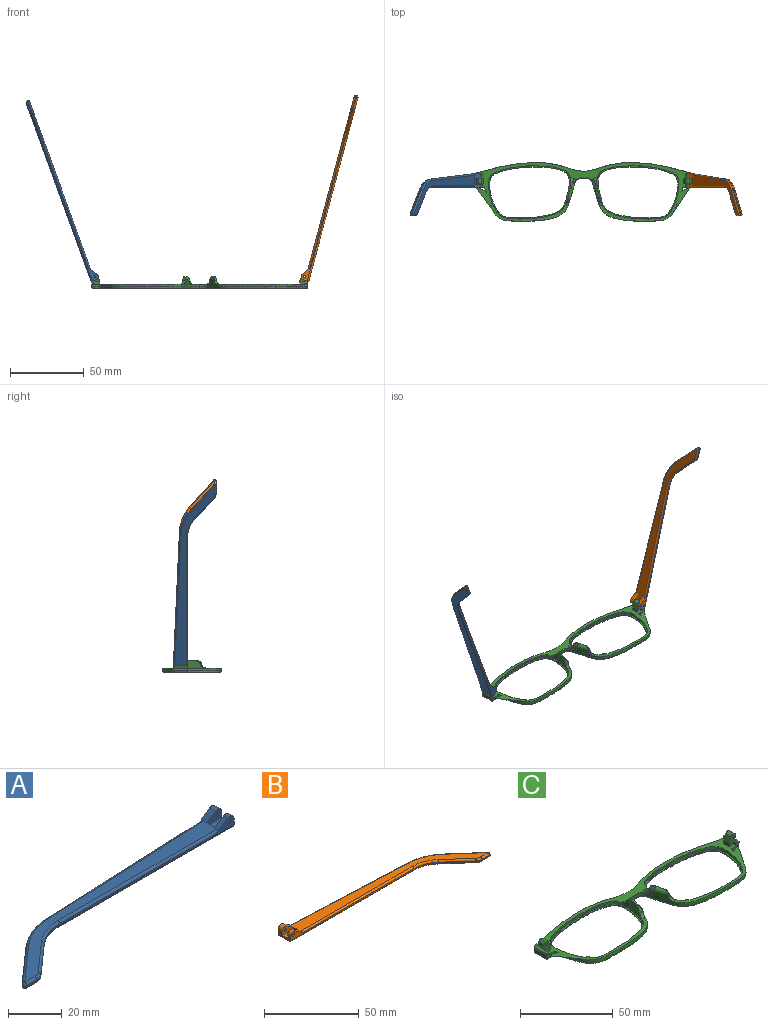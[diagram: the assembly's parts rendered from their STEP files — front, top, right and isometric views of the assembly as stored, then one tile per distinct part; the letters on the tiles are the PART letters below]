
ASSEMBLY  parts=3 mates=2
PART A: 43 faces, bbox 130.2x29.5x5.9 mm
  f0: plane 9.62x3.72mm, normal (1,0,0), area 24.7mm2, adj f1,f3,f4,f5,f10,f16,f18,f28
  f1: cylinder r=2.2mm len=3.45mm, axis (0,-1,0), area 11mm2, adj f0,f2,f4,f37
  f2: plane 6.01x3.91mm, normal (-0.55,0,0.84), area 12.7mm2, adj f1,f4,f9,f19,f37
  f3: plane 2.26x0.1mm, normal (0,0,1), area 0.1mm2, adj f0,f5,f18
  f4: plane 92.1x4.9mm, normal (0,-1,0), area 79.9mm2, adj f0,f1,f2,f14,f19,f36,f42
  f5: plane 93.42x4.13mm, normal (-0.04,1,0), area 64.8mm2, adj f0,f3,f11,f15,f17,f27,f28
  f6: plane 17.82x15.72mm, normal (-0.66,0.75,0), area 14.3mm2, adj f11,f12,f25,f30
  f7: plane 5.46x0.6mm, normal (0,-1,0), area 3.3mm2, adj f12,f13,f23,f32
  f8: plane 14.99x13.23mm, normal (0.66,-0.75,0), area 12mm2, adj f13,f14,f21,f34
  f9: plane 121.18x26.73mm, normal (0,0,1), area 627.7mm2, adj f2,f17,f19,f20,f21,f22,f23,f25
  f10: plane 129.1x27.08mm, normal (0,0,-1), area 686.5mm2, adj f0,f28,f29,f30,f32,f33,f34,f35
  f11: cylinder r=30mm len=18.52mm, axis (0,0,-1), area 12.2mm2, adj f5,f6,f26,f29
  f12: cylinder r=1mm len=1.75mm, axis (0,0,-1), area 1.5mm2, adj f6,f7,f24,f31
  f13: cylinder r=5mm len=3.31mm, axis (0,0,-1), area 2.2mm2, adj f7,f8,f22,f33
  f14: cylinder r=20mm len=13.23mm, axis (0,0,1), area 8.7mm2, adj f4,f8,f20,f35
  f15: plane 5.66x0.25mm, normal (0,0,-1), area 0.7mm2, adj f5,f17,f18
  f16: cylinder r=2.2mm len=3.45mm, axis (0,-1,0), area 14.8mm2, adj f0,f17,f18,f38
  f17: plane 6.01x3.91mm, normal (-0.55,0,0.84), area 16.9mm2, adj f5,f9,f15,f16,f18,f27,f38
  f18: plane 7.92x3.3mm, normal (0,1,0), area 15.9mm2, adj f0,f3,f15,f16,f17,f41
  f19: cylinder r=1mm len=84.18mm, axis (-1,0,0), area 131.4mm2, adj f2,f4,f9,f20
  f20: torus R=21mm, axis (0,0,1), area 23.1mm2, adj f9,f14,f19,f21
  f21: cylinder r=1mm len=15.65mm, axis (-0.75,-0.66,0), area 31.4mm2, adj f8,f9,f20,f22
  f22: torus R=4mm, axis (0,0,1), area 5.3mm2, adj f9,f13,f21,f23
  f23: cylinder r=1mm len=5.46mm, axis (-1,0,0), area 8.6mm2, adj f7,f9,f22,f24
  f24: sphere r=1mm, area 2.4mm2, adj f12,f23,f25
  f25: cylinder r=1mm len=18.48mm, axis (0.75,0.66,0), area 37.3mm2, adj f6,f9,f24,f26
  f26: torus R=29mm, axis (0,0,1), area 31.6mm2, adj f9,f11,f25,f27
  f27: cylinder r=1mm len=85.5mm, axis (1,0.04,0), area 133.5mm2, adj f5,f9,f17,f26
  f28: cylinder r=1mm len=93.46mm, axis (-1,-0.04,0), area 146.9mm2, adj f0,f5,f10,f29
  f29: torus R=29mm, axis (0,0,1), area 31.6mm2, adj f10,f11,f28,f30
  f30: cylinder r=1mm len=18.48mm, axis (-0.75,-0.66,0), area 37.3mm2, adj f6,f10,f29,f31
  f31: sphere r=1mm, area 2.4mm2, adj f12,f30,f32
  f32: cylinder r=1mm len=5.46mm, axis (1,0,0), area 8.6mm2, adj f7,f10,f31,f33
  f33: torus R=4mm, axis (0,0,1), area 5.3mm2, adj f10,f13,f32,f34
  f34: cylinder r=1mm len=15.65mm, axis (0.75,0.66,0), area 31.4mm2, adj f8,f10,f33,f35
  f35: torus R=21mm, axis (0,0,1), area 23.1mm2, adj f10,f14,f34,f36
  f36: cylinder r=1mm len=92.1mm, axis (1,0,0), area 144.7mm2, adj f0,f4,f10,f35
  f37: plane 7.92x4.7mm, normal (0,1,0), area 27mm2, adj f0,f1,f2,f39,f40,f42
  f38: plane 7.92x4.7mm, normal (0,-1,0), area 27mm2, adj f0,f16,f17,f39,f40,f41
  f39: plane 7.92x4.1mm, normal (0,0,1), area 32.5mm2, adj f0,f37,f38,f40
  f40: plane 4.1x1.4mm, normal (1,0,0), area 5.7mm2, adj f9,f37,f38,f39
  f41: cylinder r=0.5mm len=3.1mm, axis (0,-1,0), area 9.7mm2, adj f18,f38
  f42: cylinder r=0.5mm len=2.3mm, axis (0,-1,0), area 7.2mm2, adj f4,f37
PART B: 43 faces, bbox 130.2x29.5x5.9 mm
  f0: plane 9.62x3.72mm, normal (-1,0,0), area 24.7mm2, adj f1,f3,f4,f5,f10,f16,f18,f28
  f1: cylinder r=2.2mm len=3.45mm, axis (0,-1,0), area 11mm2, adj f0,f2,f4,f37
  f2: plane 6.01x3.91mm, normal (0.55,0,0.84), area 12.7mm2, adj f1,f4,f9,f19,f37
  f3: plane 2.26x0.1mm, normal (0,0,1), area 0.1mm2, adj f0,f5,f18
  f4: plane 92.1x4.9mm, normal (0,-1,0), area 78.2mm2, adj f0,f1,f2,f14,f19,f36,f42
  f5: plane 93.42x4.13mm, normal (0.04,1,0), area 64.8mm2, adj f0,f3,f11,f15,f17,f27,f28
  f6: plane 17.82x15.72mm, normal (0.66,0.75,0), area 14.3mm2, adj f11,f12,f25,f30
  f7: plane 5.46x0.6mm, normal (0,-1,0), area 3.3mm2, adj f12,f13,f23,f32
  f8: plane 14.99x13.23mm, normal (-0.66,-0.75,0), area 12mm2, adj f13,f14,f21,f34
  f9: plane 121.18x26.73mm, normal (0,0,1), area 627.7mm2, adj f2,f17,f19,f20,f21,f22,f23,f25
  f10: plane 129.1x27.08mm, normal (0,0,-1), area 686.5mm2, adj f0,f28,f29,f30,f32,f33,f34,f35
  f11: cylinder r=30mm len=18.52mm, axis (0,0,-1), area 12.2mm2, adj f5,f6,f26,f29
  f12: cylinder r=1mm len=1.75mm, axis (0,0,-1), area 1.5mm2, adj f6,f7,f24,f31
  f13: cylinder r=5mm len=3.31mm, axis (0,0,-1), area 2.2mm2, adj f7,f8,f22,f33
  f14: cylinder r=20mm len=13.23mm, axis (0,0,1), area 8.7mm2, adj f4,f8,f20,f35
  f15: plane 5.66x0.25mm, normal (0,0,-1), area 0.7mm2, adj f5,f17,f18
  f16: cylinder r=2.2mm len=3.45mm, axis (0,-1,0), area 14.8mm2, adj f0,f17,f18,f38
  f17: plane 6.01x3.91mm, normal (0.55,0,0.84), area 16.9mm2, adj f5,f9,f15,f16,f18,f27,f38
  f18: plane 7.92x3.3mm, normal (0,1,0), area 14.3mm2, adj f0,f3,f15,f16,f17,f41
  f19: cylinder r=1mm len=84.18mm, axis (1,0,0), area 131.4mm2, adj f2,f4,f9,f20
  f20: torus R=21mm, axis (0,0,1), area 23.1mm2, adj f9,f14,f19,f21
  f21: cylinder r=1mm len=15.65mm, axis (0.75,-0.66,0), area 31.4mm2, adj f8,f9,f20,f22
  f22: torus R=4mm, axis (0,0,1), area 5.3mm2, adj f9,f13,f21,f23
  f23: cylinder r=1mm len=5.46mm, axis (1,0,0), area 8.6mm2, adj f7,f9,f22,f24
  f24: sphere r=1mm, area 2.4mm2, adj f12,f23,f25
  f25: cylinder r=1mm len=18.48mm, axis (-0.75,0.66,0), area 37.3mm2, adj f6,f9,f24,f26
  f26: torus R=29mm, axis (0,0,1), area 31.6mm2, adj f9,f11,f25,f27
  f27: cylinder r=1mm len=85.5mm, axis (-1,0.04,0), area 133.5mm2, adj f5,f9,f17,f26
  f28: cylinder r=1mm len=93.46mm, axis (1,-0.04,0), area 146.9mm2, adj f0,f5,f10,f29
  f29: torus R=29mm, axis (0,0,1), area 31.6mm2, adj f10,f11,f28,f30
  f30: cylinder r=1mm len=18.48mm, axis (0.75,-0.66,0), area 37.3mm2, adj f6,f10,f29,f31
  f31: sphere r=1mm, area 2.4mm2, adj f12,f30,f32
  f32: cylinder r=1mm len=5.46mm, axis (-1,0,0), area 8.6mm2, adj f7,f10,f31,f33
  f33: torus R=4mm, axis (0,0,1), area 5.3mm2, adj f10,f13,f32,f34
  f34: cylinder r=1mm len=15.65mm, axis (-0.75,0.66,0), area 31.4mm2, adj f8,f10,f33,f35
  f35: torus R=21mm, axis (0,0,1), area 23.1mm2, adj f10,f14,f34,f36
  f36: cylinder r=1mm len=92.1mm, axis (-1,0,0), area 144.7mm2, adj f0,f4,f10,f35
  f37: plane 7.92x4.7mm, normal (0,1,0), area 25.4mm2, adj f0,f1,f2,f39,f40,f42
  f38: plane 7.92x4.7mm, normal (0,-1,0), area 25.4mm2, adj f0,f16,f17,f39,f40,f41
  f39: plane 7.92x4.1mm, normal (0,0,1), area 32.5mm2, adj f0,f37,f38,f40
  f40: plane 4.1x1.4mm, normal (-1,0,0), area 5.7mm2, adj f9,f37,f38,f39
  f41: cylinder r=0.88mm len=3.1mm, axis (0,-1,0), area 17mm2, adj f18,f38
  f42: cylinder r=0.88mm len=2.3mm, axis (0,-1,0), area 12.6mm2, adj f4,f37
PART C: 118 faces, bbox 148.1x40.9x18 mm
  f0: bspline ~1.82x1.22mm, area 0.7mm2, adj f2,f7,f37,f52
  f1: plane 147.73x40.5mm, normal (0,0,1), area 772.9mm2, adj f4,f5,f6,f7,f8,f12,f20,f23
  f2: bspline ~5.39x4.93mm, area 12.7mm2, adj f0,f7,f37,f41,f43,f52,f53
  f3: plane 4.46x1.45mm, normal (0,0,1), area 0.1mm2, adj f7,f38
  f4: plane 1.23x0.04mm, normal (0,0,1), area 0mm2, adj f1,f7,f22
  f5: plane 6.97x5.07mm, normal (0,1,0), area 22.7mm2, adj f1,f20,f21,f25,f27,f28,f30,f31
  f6: plane 3.2x2.36mm, normal (0,-1,0), area 5.7mm2, adj f1,f20,f26,f29
  f7: extruded ~73.26x39.84mm, area 292.7mm2, adj f0,f1,f2,f3,f4,f8,f13,f14
  f8: extruded ~35.39x5.69mm, area 72.2mm2, adj f1,f7,f18,f67
  f9: plane 144.78x37.85mm, normal (0,0,-1), area 478.1mm2, adj f13,f15,f17,f18,f19,f71,f73,f75
  f10: plane 56.31x36.53mm, normal (0,0,1), area 124.8mm2, adj f11,f19
  f11: extruded ~55.63x36.1mm, area 160.7mm2, adj f10,f12
  f12: extruded ~55.63x36.1mm, area 220.4mm2, adj f1,f11,f39,f40,f41,f42,f43,f44
  f13: bspline ~73.27x30.39mm, area 161.7mm2, adj f7,f9,f14,f71
  f14: bspline ~1x1mm, area 0.8mm2, adj f7,f13,f15
  f15: bspline ~8.99x1.23mm, area 12.6mm2, adj f7,f9,f14,f16
  f16: bspline ~1.04x1mm, area 0.7mm2, adj f7,f15,f17
  f17: bspline ~45.86x8.59mm, area 59.8mm2, adj f7,f9,f16,f18
  f18: bspline ~37.01x6.7mm, area 56.6mm2, adj f8,f9,f17,f76
  f19: bspline ~56.15x36.68mm, area 237.6mm2, adj f9,f10
  f20: plane 4x2.36mm, normal (-1,0,0), area 9.5mm2, adj f1,f5,f6,f21
  f21: plane 4x0.02mm, normal (0.34,0,0.94), area 0.1mm2, adj f5,f20,f28
  f22: plane 2.76x2.53mm, normal (0,-1,0), area 3.9mm2, adj f4,f26,f27,f35,f56
  f23: plane 7.67x1.6mm, normal (0.94,0,-0.34), area 13mm2, adj f1,f35,f36,f56
  f24: plane 2.1x1.69mm, normal (0,1,0), area 2.8mm2, adj f1,f25,f27,f36,f56
  f25: plane 3.3x2.1mm, normal (-1,0,0), area 6.9mm2, adj f1,f5,f24,f27
  f26: plane 2.35x2.1mm, normal (-1,0,0), area 4.9mm2, adj f1,f6,f22,f27,f29
  f27: plane 9.65x1.24mm, normal (0,0,1), area 8.2mm2, adj f5,f22,f24,f25,f26,f29,f30,f56
  f28: plane 4x3.31mm, normal (-0.94,0,0.34), area 14.1mm2, adj f5,f21,f29,f32
  f29: plane 5.77x5.06mm, normal (0,-1,0), area 17mm2, adj f6,f26,f27,f28,f30,f31,f32,f33
  f30: plane 4x2.21mm, normal (0.94,0,-0.34), area 9.4mm2, adj f5,f27,f29,f33
  f31: plane 4x0.01mm, normal (0.34,0,0.94), area 0mm2, adj f5,f29,f32,f33
  f32: cylinder r=1.98mm len=4mm, axis (0,1,0), area 12.4mm2, adj f5,f28,f29,f31
  f33: cylinder r=1.98mm len=4mm, axis (0,-1,0), area 12.4mm2, adj f5,f29,f30,f31
  f34: cylinder r=0.88mm len=4mm, axis (0,-1,0), area 22mm2, adj f5,f29
  f35: cone r=1mm half-angle=20deg, axis (0,0,1), area 2.3mm2, adj f1,f22,f23,f56
  f36: cylinder r=1mm len=2.28mm, axis (-0.34,0,-0.94), area 3mm2, adj f1,f23,f24,f56
  f37: extruded ~3.67x3.11mm, area 5.9mm2, adj f0,f2,f7,f59
  f38: extruded ~4.44x3.32mm, area 15.1mm2, adj f3,f7,f42,f43,f55
  f39: extruded ~4.98x1.36mm, area 6.6mm2, adj f12,f41
  f40: plane 3.63x0.97mm, normal (0,0,1), area 0.3mm2, adj f12,f41,f43
  f41: bspline ~15.5x15.35mm, area 6.4mm2, adj f2,f12,f39,f40,f54
  f42: bspline ~7.26x7.26mm, area 6.3mm2, adj f12,f38,f43,f55
  f43: bspline ~10.29x4.84mm, area 21.4mm2, adj f2,f7,f12,f38,f40,f42
  f44: plane 2.88x1.51mm, normal (0,0,-1), area 1.8mm2, adj f12,f45
  f45: cylinder r=2.28mm len=2.86mm, axis (0,0,1), area 1.8mm2, adj f1,f12,f44,f54
  f46: plane 2.5x1.83mm, normal (0,0,-1), area 1.7mm2, adj f12,f47
  f47: cylinder r=2.28mm len=2.47mm, axis (0,0,1), area 1.7mm2, adj f1,f12,f46
  f48: plane 1.79x1.31mm, normal (0,0,-1), area 0.9mm2, adj f12,f49
  f49: cylinder r=1.3mm len=1.78mm, axis (0,0,1), area 1.3mm2, adj f1,f12,f48
  f50: plane 1.95x1.68mm, normal (0,0,-1), area 1.5mm2, adj f12,f51
  f51: cylinder r=1.3mm len=1.93mm, axis (0,0,1), area 1.5mm2, adj f1,f12,f50
  f52: bspline ~2.66x2.04mm, area 1.9mm2, adj f0,f2,f7,f53,f58
  f53: bspline ~3.55x3.47mm, area 3.7mm2, adj f1,f2,f52,f54,f58
  f54: bspline ~5.1x3.97mm, area 7.6mm2, adj f1,f12,f41,f45,f53
  f55: bspline ~3.7x3.66mm, area 7.8mm2, adj f1,f7,f12,f38,f42
  f56: plane 9.71x1.44mm, normal (0.34,0,0.94), area 13.9mm2, adj f22,f23,f24,f27,f35,f36
  f57: bspline ~6.38x2.14mm, area 2.6mm2, adj f1,f7,f58,f115
  f58: bspline ~2.1x1.46mm, area 0.6mm2, adj f7,f52,f53,f57
  f59: bspline ~5.24x1.75mm, area 0mm2, adj f7,f37
  f60: bspline ~2.19x1.4mm, area 0.7mm2, adj f61,f66,f95,f110
  f61: bspline ~6.1x4.93mm, area 12.6mm2, adj f60,f66,f95,f99,f101,f110,f111
  f62: plane 4.46x1.45mm, normal (0,0,1), area 0.1mm2, adj f66,f96
  f63: plane 1.23x0.04mm, normal (0,0,1), area 0mm2, adj f1,f66,f80
  f64: plane 6.97x5.07mm, normal (0,1,0), area 22.7mm2, adj f1,f78,f79,f83,f85,f86,f88,f89
  f65: plane 3.2x2.36mm, normal (0,-1,0), area 5.7mm2, adj f1,f78,f84,f87
  f66: extruded ~73.26x39.84mm, area 292.7mm2, adj f1,f7,f60,f61,f62,f63,f67,f71
  f67: extruded ~35.39x5.69mm, area 72.2mm2, adj f1,f8,f66,f76
  f68: plane 56.31x36.53mm, normal (0,0,1), area 124.8mm2, adj f69,f77
  f69: extruded ~55.63x36.1mm, area 160.7mm2, adj f68,f70
  f70: extruded ~55.63x36.1mm, area 220.4mm2, adj f1,f69,f97,f98,f99,f100,f101,f102
  f71: bspline ~73.83x30.39mm, area 161.7mm2, adj f9,f13,f66,f72
  f72: bspline ~1x1mm, area 0.8mm2, adj f66,f71,f73
  f73: bspline ~8.99x1.23mm, area 12.6mm2, adj f9,f66,f72,f74
  f74: bspline ~1.04x1mm, area 0.8mm2, adj f66,f73,f75
  f75: bspline ~45.86x8.59mm, area 59.8mm2, adj f9,f66,f74,f76
  f76: bspline ~37.01x6.7mm, area 56.6mm2, adj f9,f18,f67,f75
  f77: bspline ~56.15x36.68mm, area 237.6mm2, adj f9,f68
  f78: plane 4x2.36mm, normal (1,0,0), area 9.5mm2, adj f1,f64,f65,f79
  f79: plane 4x0.02mm, normal (-0.34,0,0.94), area 0.1mm2, adj f64,f78,f86
  f80: plane 2.76x2.53mm, normal (0,-1,0), area 3.9mm2, adj f63,f84,f85,f93,f114
  f81: plane 7.67x1.6mm, normal (-0.94,0,-0.34), area 13mm2, adj f1,f93,f94,f114
  f82: plane 2.1x1.69mm, normal (0,1,0), area 2.8mm2, adj f1,f83,f85,f94,f114
  f83: plane 3.3x2.1mm, normal (1,0,0), area 6.9mm2, adj f1,f64,f82,f85
  f84: plane 2.35x2.1mm, normal (1,0,0), area 4.9mm2, adj f1,f65,f80,f85,f87
  f85: plane 9.65x1.24mm, normal (0,0,1), area 8.2mm2, adj f64,f80,f82,f83,f84,f87,f88,f114
  f86: plane 4x3.31mm, normal (0.94,0,0.34), area 14.1mm2, adj f64,f79,f87,f90
  f87: plane 5.77x5.06mm, normal (0,-1,0), area 17mm2, adj f65,f84,f85,f86,f88,f89,f90,f91
  f88: plane 4x2.21mm, normal (-0.94,0,-0.34), area 9.4mm2, adj f64,f85,f87,f91
  f89: plane 4x0.01mm, normal (-0.34,0,0.94), area 0mm2, adj f64,f87,f90,f91
  f90: cylinder r=1.98mm len=4mm, axis (0,1,0), area 12.4mm2, adj f64,f86,f87,f89
  f91: cylinder r=1.98mm len=4mm, axis (0,-1,0), area 12.4mm2, adj f64,f87,f88,f89
  f92: cylinder r=0.88mm len=4mm, axis (0,-1,0), area 22mm2, adj f64,f87
  f93: cone r=1mm half-angle=20deg, axis (0,0,1), area 2.3mm2, adj f1,f80,f81,f114
  f94: cylinder r=1mm len=2.28mm, axis (0.34,0,-0.94), area 3mm2, adj f1,f81,f82,f114
  f95: extruded ~3.67x3.11mm, area 5.9mm2, adj f60,f61,f66,f117
  f96: extruded ~4.44x3.32mm, area 15.1mm2, adj f62,f66,f100,f101,f113
  f97: extruded ~4.98x1.36mm, area 6.6mm2, adj f70,f99
  f98: plane 3.63x0.97mm, normal (0,0,1), area 0.3mm2, adj f70,f99,f101
  f99: bspline ~15.5x15.35mm, area 6.4mm2, adj f61,f70,f97,f98,f112
  f100: bspline ~7.26x7.26mm, area 6.2mm2, adj f70,f96,f101,f113
  f101: bspline ~10.29x4.84mm, area 21.5mm2, adj f61,f66,f70,f96,f98,f100
  f102: plane 2.88x1.51mm, normal (0,0,-1), area 1.8mm2, adj f70,f103
  f103: cylinder r=2.28mm len=2.86mm, axis (0,0,1), area 1.8mm2, adj f1,f70,f102,f112
  f104: plane 2.5x1.83mm, normal (0,0,-1), area 1.7mm2, adj f70,f105
  f105: cylinder r=2.28mm len=2.47mm, axis (0,0,1), area 1.7mm2, adj f1,f70,f104
  f106: plane 1.79x1.31mm, normal (0,0,-1), area 0.9mm2, adj f70,f107
  f107: cylinder r=1.3mm len=1.78mm, axis (0,0,1), area 1.3mm2, adj f1,f70,f106
  f108: plane 1.95x1.68mm, normal (0,0,-1), area 1.5mm2, adj f70,f109
  f109: cylinder r=1.3mm len=1.93mm, axis (0,0,1), area 1.5mm2, adj f1,f70,f108
  f110: bspline ~2.65x2.03mm, area 1.9mm2, adj f60,f61,f66,f111,f116
  f111: bspline ~3.55x3.47mm, area 3.7mm2, adj f1,f61,f110,f112,f116
  f112: bspline ~4.88x3.94mm, area 7.6mm2, adj f1,f70,f99,f103,f111
  f113: bspline ~3.7x3.66mm, area 7.8mm2, adj f1,f66,f70,f96,f100
  f114: plane 9.71x1.44mm, normal (-0.34,0,0.94), area 13.9mm2, adj f80,f81,f82,f85,f93,f94
  f115: bspline ~6.38x2.14mm, area 2.6mm2, adj f1,f57,f66,f116
  f116: bspline ~2.1x1.46mm, area 0.6mm2, adj f66,f110,f111,f115
  f117: bspline ~5.24x1.75mm, area 0mm2, adj f66,f95
PLACE A rot(axis=(0,1,0),70deg) t=(-104.56,-3.6,76.36)mm
PLACE B rot(axis=(0,-1,0),75deg) t=(48.41,-3.6,-41.26)mm
PLACE C t=(-9.64,1.01,14.58)mm
MATE revolute A.f1 <-> C.f90  axis (0,-1,0) through (-80.68,4.86,21.57)mm
MATE revolute B.f41 <-> C.f33  axis (0,-1,0) through (61.41,4.86,21.57)mm
